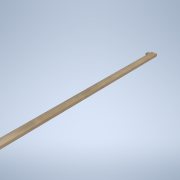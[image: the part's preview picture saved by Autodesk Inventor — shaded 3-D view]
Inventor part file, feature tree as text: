
AUTODESK INVENTOR PART (.ipt)
format: ipt  version: 2021 (Build 250183000, 183)  size: 138,240 bytes
history: native  units: mm
features: extrude x1, sketch x1
ambient origin geometry x8: Origin, YZ Plane, XZ Plane, XY Plane, X Axis, Y Axis, Z Axis, Center Point
bodies: Solid1 (feature_tree)
feature tree (2):
  extrude  "Extrusion1"  Depth=3.0mm
  sketch  "Sketch1"  dims[d4=3.0mm d5=0.0mm d10=3.0mm d16=60.0mm d18=38.0mm d19=10.0mm d21=10.0mm d11=0.5mm d12=0.872665mm d13=0.5mm d14=0.872665mm]
